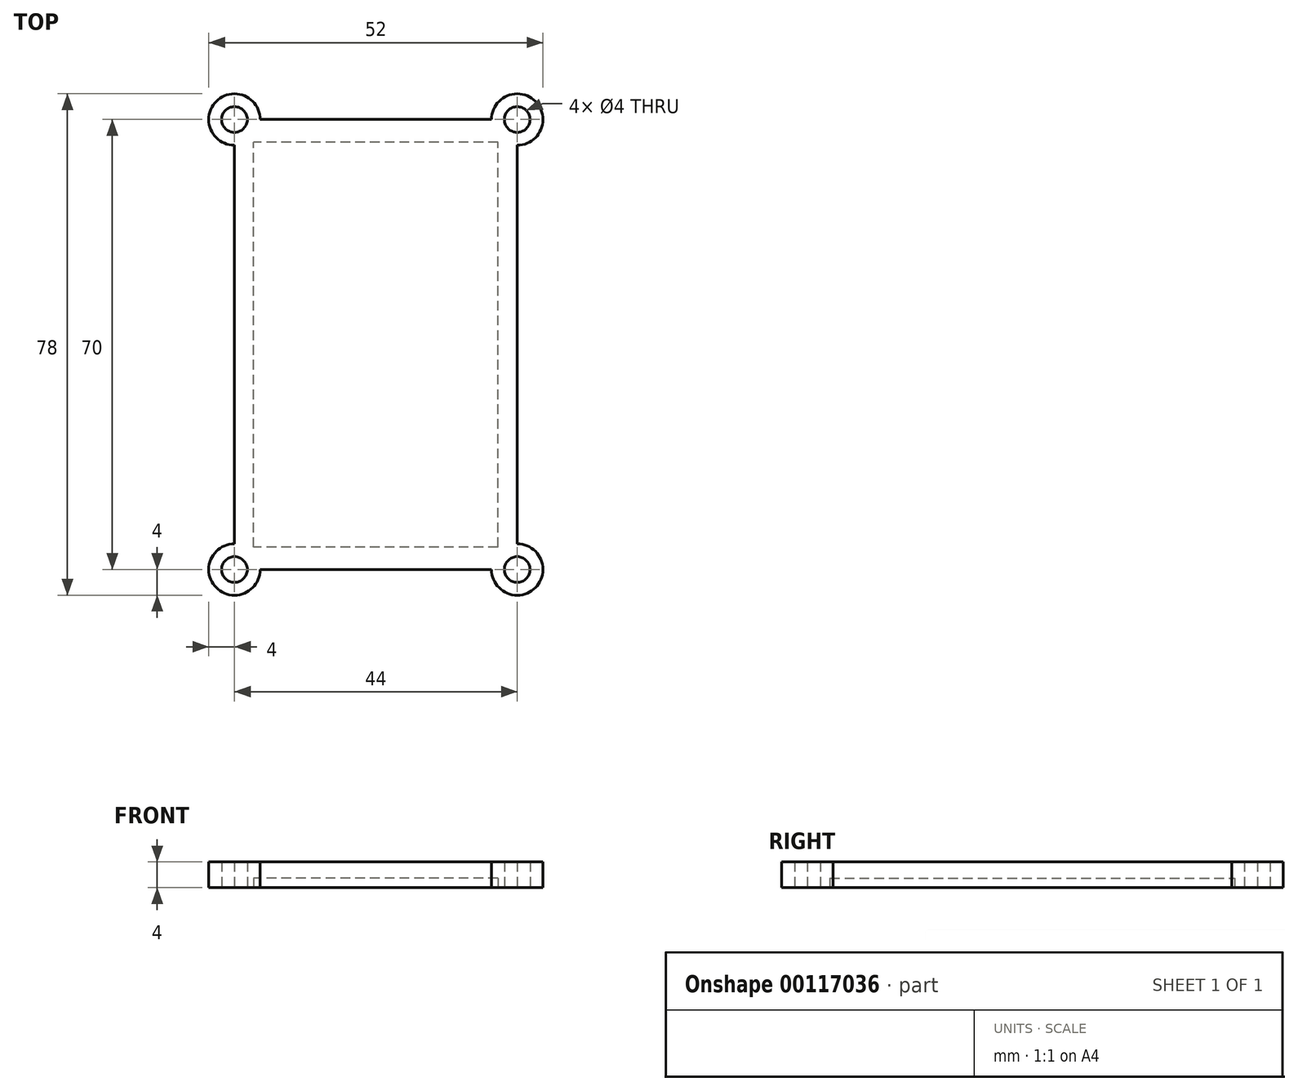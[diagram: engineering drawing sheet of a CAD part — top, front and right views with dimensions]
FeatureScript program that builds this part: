
annotation { "Feature Type Name" : "Feature", "Feature Type Description" : "" }
export const myFeature = defineFeature(function(context is Context, id is Id, definition is map)
    precondition{}
    {
        {
            var Q0;
            Q0=qCreatedBy(makeId("Top.planeOp"),FACE);
            var sketch = newSketch(context, id + "F0", { "sketchPlane" : qUnion([Q0])});
            skLineSegment(sketch, "E0.bottom", {"start": v(22, 35) * mm, "end": v(-22, 35) * mm});
            skLineSegment(sketch, "E0.top", {"start": v(22, -35) * mm, "end": v(-22, -35) * mm});
            skLineSegment(sketch, "E0.left", {"start": v(22, 35) * mm, "end": v(22, -35) * mm});
            skLineSegment(sketch, "E0.right", {"start": v(-22, 35) * mm, "end": v(-22, -35) * mm});
            skPoint(sketch, "E0.middle", {"position": v(0, 0) * mm});
            skCircle(sketch, "E1", {"center": v(-22, 35) * mm, "radius": 4 * mm});
            skCircle(sketch, "E2", {"center": v(22, 35) * mm, "radius": 4 * mm});
            skCircle(sketch, "E3", {"center": v(22, -35) * mm, "radius": 4 * mm});
            skCircle(sketch, "E4", {"center": v(-22, -35) * mm, "radius": 4 * mm});
            skSolve(sketch);
        }
        {
            var Q0;
            Q0 = qSketchRegion(id + "F0", true);
            extrude(context, id + "F1", {"entities" : qUnion([Q0]), "depth" : 4 * mm});
        }
        {
            var Q0;
            Q0=makeQuery(id+"F1.opExtrude","CAP_FACE",FACE,{"disambiguationData":[OSD([sQuery(id+"F0.wireOp",EDGE,"E0.bottom"),sQuery(id+"F0.wireOp",EDGE,"E0.top"),sQuery(id+"F0.wireOp",EDGE,"E0.left"),sQuery(id+"F0.wireOp",EDGE,"E0.right"),sQuery(id+"F0.wireOp",EDGE,"E1"),sQuery(id+"F0.wireOp",EDGE,"E2"),sQuery(id+"F0.wireOp",EDGE,"E3"),sQuery(id+"F0.wireOp",EDGE,"E4")])],"isStart":true});
            var sketch = newSketch(context, id + "F2", { "sketchPlane" : qUnion([Q0])});
            skLineSegment(sketch, "E5.bottom", {"start": v(19, 31.5) * mm, "end": v(-19, 31.5) * mm});
            skLineSegment(sketch, "E5.top", {"start": v(19, -31.5) * mm, "end": v(-19, -31.5) * mm});
            skLineSegment(sketch, "E5.left", {"start": v(19, 31.5) * mm, "end": v(19, -31.5) * mm});
            skLineSegment(sketch, "E5.right", {"start": v(-19, 31.5) * mm, "end": v(-19, -31.5) * mm});
            skPoint(sketch, "E5.middle", {"position": v(0, 0) * mm});
            skSolve(sketch);
        }
        {
            var Q0;
            Q0 = qSketchRegion(id + "F2", true);
            extrude(context, id + "F3", {"entities" : qUnion([Q0]), "operationType" : NewBodyOperationType.REMOVE, "oppositeDirection" : true, "depth" : 1.5 * mm});
        }
        {
            var Q0;
            Q0=makeQuery(id+"F1.opExtrude","CAP_FACE",FACE,{"disambiguationData":[OSD([sQuery(id+"F0.wireOp",EDGE,"E0.bottom"),sQuery(id+"F0.wireOp",EDGE,"E0.top"),sQuery(id+"F0.wireOp",EDGE,"E0.left"),sQuery(id+"F0.wireOp",EDGE,"E0.right"),sQuery(id+"F0.wireOp",EDGE,"E1"),sQuery(id+"F0.wireOp",EDGE,"E2"),sQuery(id+"F0.wireOp",EDGE,"E3"),sQuery(id+"F0.wireOp",EDGE,"E4")])],"isStart":true});
            var sketch = newSketch(context, id + "F4", { "sketchPlane" : qUnion([Q0])});
            skCircle(sketch, "E6", {"center": v(-22, 35) * mm, "radius": 2 * mm});
            skCircle(sketch, "E7", {"center": v(22, 35) * mm, "radius": 2 * mm});
            skCircle(sketch, "E8", {"center": v(-22, -35) * mm, "radius": 2 * mm});
            skCircle(sketch, "E9", {"center": v(22, -35) * mm, "radius": 2 * mm});
            skSolve(sketch);
        }
        {
            var Q0;
            Q0 = qSketchRegion(id + "F4", true);
            extrude(context, id + "F5", {"entities" : qUnion([Q0]), "operationType" : NewBodyOperationType.REMOVE, "endBound" : BoundingType.UP_TO_NEXT, "oppositeDirection" : true, "depth" : 25 * mm});
        }
    });
